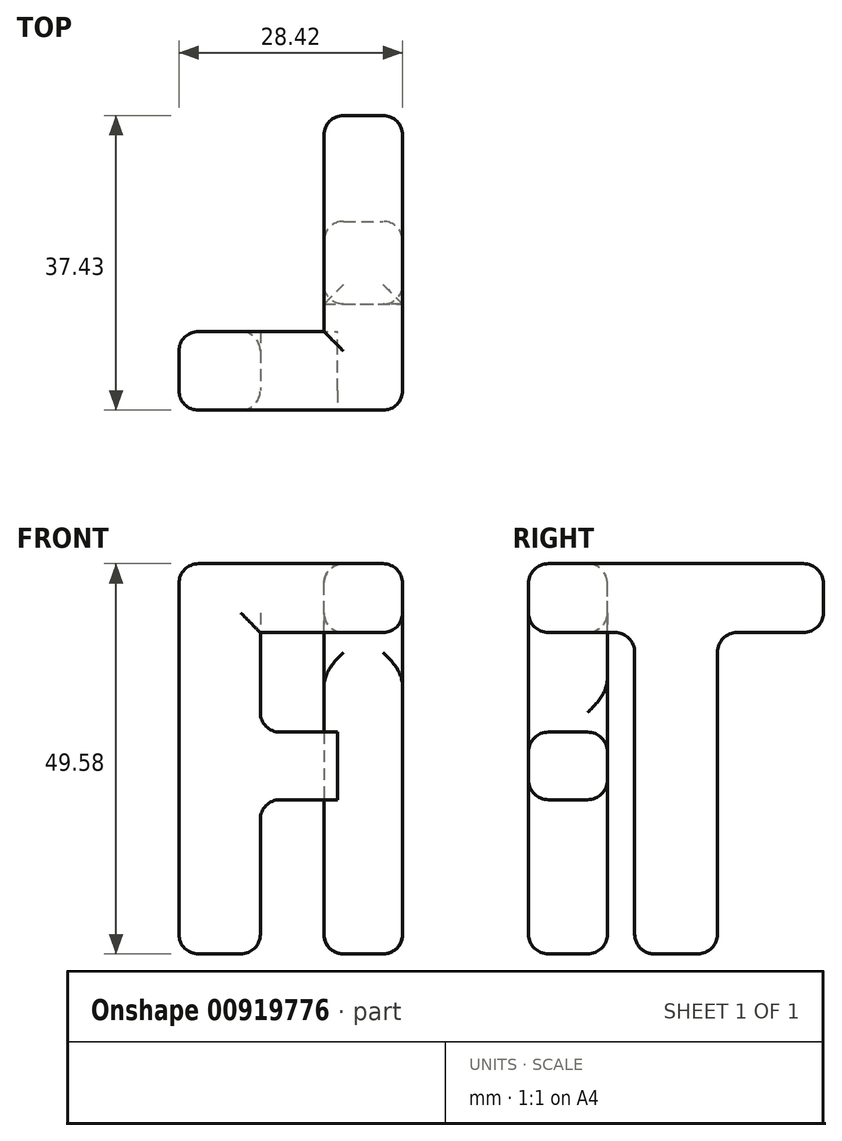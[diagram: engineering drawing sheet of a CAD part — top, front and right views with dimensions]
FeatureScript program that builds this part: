
annotation { "Feature Type Name" : "Feature", "Feature Type Description" : "" }
export const myFeature = defineFeature(function(context is Context, id is Id, definition is map)
    precondition{}
    {
        {
            var Q0;
            Q0=qCreatedBy(makeId("Front.planeOp"),FACE);
            var sketch = newSketch(context, id + "F0", { "sketchPlane" : qUnion([Q0])});
            skText(sketch, "E0", { "text": "F", "fontName": "NotoSans-Bold.ttf"});
            const initialGuessF0  = {"E0": [-0.03238, -0.0213, 1, 0, 0.05]};
            skSetInitialGuess(sketch, initialGuessF0);
            skSolve(sketch);
        }
        {
            var Q0;
            Q0=makeQuery(id+"F0.imprint","IMPRINT",FACE,{"disambiguationData":[TD([[makeQuery(id+"F0.imprint","IMPRINT",EDGE,{"derivedFrom":sQuery(id+"F0.wireOp",EDGE,"E0.sketch_text.stroke-0")}),-1.0]])]});
            extrude(context, id + "F1", {"entities" : qUnion([Q0]), "depth" : -10 * mm, "offsetDistance" : 25 * mm});
        }
        {
            var Q0;
            Q0=qCreatedBy(makeId("Right.planeOp"),FACE);
            var sketch = newSketch(context, id + "F2", { "sketchPlane" : qUnion([Q0])});
            skText(sketch, "E1", { "text": "T", "fontName": "OpenSans-Bold.ttf"});
            const initialGuessF2  = {"E1": [0.02709, -0.02241, 1, 0, 0.05]};
            skSetInitialGuess(sketch, initialGuessF2);
            skSolve(sketch);
        }
        {
            var Q0;
            Q0 = qSketchRegion(id + "F2", true);
            extrude(context, id + "F3", {"entities" : qUnion([Q0]), "depth" : -10 * mm, "offsetDistance" : 25 * mm});
        }
        {
            var Q0;
            Q0=makeQuery(id+"F3.opExtrude","SWEPT_BODY",BODY,{"disambiguationData":[OSD([sQuery(id+"F2.wireOp",EDGE,"E1.sketch_text.stroke-0"),sQuery(id+"F2.wireOp",EDGE,"E1.sketch_text.stroke-1"),sQuery(id+"F2.wireOp",EDGE,"E1.sketch_text.stroke-2"),sQuery(id+"F2.wireOp",EDGE,"E1.sketch_text.stroke-3"),sQuery(id+"F2.wireOp",EDGE,"E1.sketch_text.stroke-4"),sQuery(id+"F2.wireOp",EDGE,"E1.sketch_text.stroke-5"),sQuery(id+"F2.wireOp",EDGE,"E1.sketch_text.stroke-6"),sQuery(id+"F2.wireOp",EDGE,"E1.sketch_text.stroke-7")])]});
            var Q1;
            Q1=makeQuery(id+"F3.opExtrude","CAP_VERTEX",VERTEX,{"disambiguationData":[OSD([sQuery(id+"F2.wireOp",EDGE,"E1.sketch_text.stroke-3"),sQuery(id+"F2.wireOp",EDGE,"E1.sketch_text.stroke-4")])],"isStart":true});
            var Q2;
            Q2=makeQuery(id+"F1.opExtrude","CAP_VERTEX",VERTEX,{"disambiguationData":[OSD([sQuery(id+"F0.wireOp",EDGE,"E0.sketch_text.stroke-2"),sQuery(id+"F0.wireOp",EDGE,"E0.sketch_text.stroke-3")])],"isStart":true});
            transform(context, id + "F4", {"entities" : qUnion([Q0]), "transformType" : TransformType.TRANSLATION_ENTITY, "oppositeDirectionEntity" : false, "transformLine" : qUnion([Q1, Q2]), "makeCopy" : false});
        }
        {
            var Q0;
            Q0=makeQuery(id+"F1.opExtrude","SWEPT_FACE",FACE,{"disambiguationData":[OSD([sQuery(id+"F0.wireOp",EDGE,"E0.sketch_text.stroke-7")])]});
            var sketch = newSketch(context, id + "F5", { "sketchPlane" : qUnion([Q0])});
            skLineSegment(sketch, "E2.bottom", {"start": v(0, 6.88) * mm, "end": v(10, 6.88) * mm});
            skLineSegment(sketch, "E2.top", {"start": v(0, -1.7) * mm, "end": v(10, -1.7) * mm});
            skLineSegment(sketch, "E2.left", {"start": v(0, 6.88) * mm, "end": v(0, -1.7) * mm});
            skLineSegment(sketch, "E2.right", {"start": v(10, 6.88) * mm, "end": v(10, -1.7) * mm});
            skSolve(sketch);
        }
        {
            var Q0;
            Q0 = qSketchRegion(id + "F5", true);
            extrude(context, id + "F6", {"entities" : qUnion([Q0]), "depth" : -7 * mm, "offsetDistance" : 25 * mm});
        }
        {
            var Q0;
            Q0=makeQuery(id+"F6.opExtrude","SWEPT_BODY",BODY,{"disambiguationData":[OSD([sQuery(id+"F5.wireOp",EDGE,"E2.bottom"),sQuery(id+"F5.wireOp",EDGE,"E2.top"),sQuery(id+"F5.wireOp",EDGE,"E2.left"),sQuery(id+"F5.wireOp",EDGE,"E2.right")])]});
            var Q1;
            Q1=makeQuery(id+"F1.opExtrude","SWEPT_BODY",BODY,{"disambiguationData":[OSD([sQuery(id+"F0.wireOp",EDGE,"E0.sketch_text.stroke-0"),sQuery(id+"F0.wireOp",EDGE,"E0.sketch_text.stroke-1"),sQuery(id+"F0.wireOp",EDGE,"E0.sketch_text.stroke-2"),sQuery(id+"F0.wireOp",EDGE,"E0.sketch_text.stroke-3"),sQuery(id+"F0.wireOp",EDGE,"E0.sketch_text.stroke-4"),sQuery(id+"F0.wireOp",EDGE,"E0.sketch_text.stroke-5"),sQuery(id+"F0.wireOp",EDGE,"E0.sketch_text.stroke-6"),sQuery(id+"F0.wireOp",EDGE,"E0.sketch_text.stroke-7"),sQuery(id+"F0.wireOp",EDGE,"E0.sketch_text.stroke-8"),sQuery(id+"F0.wireOp",EDGE,"E0.sketch_text.stroke-9")])]});
            booleanBodies(context, id + "F7", {"operationType" : BooleanOperationType.SUBTRACTION, "tools" : qUnion([Q0]), "targets" : qUnion([Q1])});
        }
        {
            var Q0;
            Q0=makeQuery(id+"F1.opExtrude","SWEPT_BODY",BODY,{"disambiguationData":[OSD([sQuery(id+"F0.wireOp",EDGE,"E0.sketch_text.stroke-0"),sQuery(id+"F0.wireOp",EDGE,"E0.sketch_text.stroke-1"),sQuery(id+"F0.wireOp",EDGE,"E0.sketch_text.stroke-2"),sQuery(id+"F0.wireOp",EDGE,"E0.sketch_text.stroke-3"),sQuery(id+"F0.wireOp",EDGE,"E0.sketch_text.stroke-4"),sQuery(id+"F0.wireOp",EDGE,"E0.sketch_text.stroke-5"),sQuery(id+"F0.wireOp",EDGE,"E0.sketch_text.stroke-6"),sQuery(id+"F0.wireOp",EDGE,"E0.sketch_text.stroke-7"),sQuery(id+"F0.wireOp",EDGE,"E0.sketch_text.stroke-8"),sQuery(id+"F0.wireOp",EDGE,"E0.sketch_text.stroke-9")])]});
            var Q1;
            Q1=makeQuery(id+"F3.opExtrude","SWEPT_BODY",BODY,{"disambiguationData":[OSD([sQuery(id+"F2.wireOp",EDGE,"E1.sketch_text.stroke-0"),sQuery(id+"F2.wireOp",EDGE,"E1.sketch_text.stroke-1"),sQuery(id+"F2.wireOp",EDGE,"E1.sketch_text.stroke-2"),sQuery(id+"F2.wireOp",EDGE,"E1.sketch_text.stroke-3"),sQuery(id+"F2.wireOp",EDGE,"E1.sketch_text.stroke-4"),sQuery(id+"F2.wireOp",EDGE,"E1.sketch_text.stroke-5"),sQuery(id+"F2.wireOp",EDGE,"E1.sketch_text.stroke-6"),sQuery(id+"F2.wireOp",EDGE,"E1.sketch_text.stroke-7")])]});
            booleanBodies(context, id + "F8", {"operationType" : BooleanOperationType.UNION, "tools" : qUnion([Q0, Q1])});
        }
        {
            var Q0;
            Q0=makeQuery(id+"F1.opExtrude","SWEPT_FACE",FACE,{"disambiguationData":[OSD([sQuery(id+"F0.wireOp",EDGE,"E0.sketch_text.stroke-4")])]});
            var sketch = newSketch(context, id + "F9", { "sketchPlane" : qUnion([Q0])});
            skLineSegment(sketch, "E3.bottom", {"start": v(-15.8, -10) * mm, "end": v(-7.72, -10) * mm});
            skLineSegment(sketch, "E3.top", {"start": v(-15.8, 0) * mm, "end": v(-7.72, 0) * mm});
            skLineSegment(sketch, "E3.left", {"start": v(-15.8, -10) * mm, "end": v(-15.8, 0) * mm});
            skLineSegment(sketch, "E3.right", {"start": v(-7.72, -10) * mm, "end": v(-7.72, 0) * mm});
            skSolve(sketch);
        }
        {
            var Q0;
            Q0=makeQuery(id+"F9.imprint","IMPRINT",FACE,{"disambiguationData":[TD([[makeQuery(id+"F9.imprint","IMPRINT",EDGE,{"derivedFrom":sQuery(id+"F9.wireOp",EDGE,"E3.bottom")}),-1.0]])]});
            var Q1;
            Q1=makeQuery(id+"F3.opExtrude","SWEPT_FACE",FACE,{"disambiguationData":[OSD([sQuery(id+"F2.wireOp",EDGE,"E1.sketch_text.stroke-2")])]});
            extrude(context, id + "F10", {"entities" : qUnion([Q0]), "operationType" : NewBodyOperationType.ADD, "endBound" : BoundingType.UP_TO_SURFACE, "depth" : 25 * mm, "endBoundEntityFace" : qUnion([Q1]), "offsetDistance" : 25 * mm});
        }
        {
            var Q0;
            Q0=makeQuery(id+"F10.boolean.opBoolean","MERGE",EDGE,{"derivedFrom":[makeQuery(id+"F3.opExtrude","SWEPT_EDGE",EDGE,{"disambiguationData":[OSD([sQuery(id+"F2.wireOp",EDGE,"E1.sketch_text.stroke-2"),sQuery(id+"F2.wireOp",EDGE,"E1.sketch_text.stroke-3")])]}),makeQuery(id+"F10.opExtrude","CAP_EDGE",EDGE,{"disambiguationData":[OSD([sQuery(id+"F9.wireOp",EDGE,"E3.top")])],"isStart":false})]});
            var Q1;
            Q1=makeQuery(id+"F1.opExtrude","CAP_EDGE",EDGE,{"disambiguationData":[OSD([sQuery(id+"F0.wireOp",EDGE,"E0.sketch_text.stroke-5")])],"isStart":true});
            var Q2;
            Q2=makeQuery(id+"F3.opExtrude","CAP_EDGE",EDGE,{"disambiguationData":[OSD([sQuery(id+"F2.wireOp",EDGE,"E1.sketch_text.stroke-2")])],"isStart":true});
            var Q3;
            Q3=makeQuery(id+"F3.opExtrude","SWEPT_EDGE",EDGE,{"disambiguationData":[OSD([sQuery(id+"F2.wireOp",EDGE,"E1.sketch_text.stroke-1"),sQuery(id+"F2.wireOp",EDGE,"E1.sketch_text.stroke-2")])]});
            var Q4;
            Q4=makeQuery(id+"F10.opExtrude","CAP_EDGE",EDGE,{"disambiguationData":[OSD([sQuery(id+"F9.wireOp",EDGE,"E3.bottom")])],"isStart":false});
            var Q5;
            Q5=makeQuery(id+"F3.opExtrude","CAP_EDGE",EDGE,{"disambiguationData":[OSD([sQuery(id+"F2.wireOp",EDGE,"E1.sketch_text.stroke-2")])],"isStart":false});
            var Q6;
            Q6=makeQuery(id+"F10.opExtrude","CAP_EDGE",EDGE,{"disambiguationData":[OSD([sQuery(id+"F9.wireOp",EDGE,"E3.left")])],"isStart":false});
            var Q7;
            Q7=makeQuery(id+"F8.opBoolean","MERGE",EDGE,{"derivedFrom":[makeQuery(id+"F1.opExtrude","CAP_EDGE",EDGE,{"disambiguationData":[OSD([sQuery(id+"F0.wireOp",EDGE,"E0.sketch_text.stroke-3")])],"isStart":true}),makeQuery(id+"F3.opExtrude","CAP_EDGE",EDGE,{"disambiguationData":[OSD([sQuery(id+"F2.wireOp",EDGE,"E1.sketch_text.stroke-3")])],"isStart":true})]});
            var Q8;
            Q8=makeQuery(id+"F1.opExtrude","CAP_EDGE",EDGE,{"disambiguationData":[OSD([sQuery(id+"F0.wireOp",EDGE,"E0.sketch_text.stroke-2")])],"isStart":true});
            var Q9;
            Q9=makeQuery(id+"F8.opBoolean","MERGE",EDGE,{"derivedFrom":[makeQuery(id+"F1.opExtrude","SWEPT_EDGE",EDGE,{"disambiguationData":[OSD([sQuery(id+"F0.wireOp",EDGE,"E0.sketch_text.stroke-2"),sQuery(id+"F0.wireOp",EDGE,"E0.sketch_text.stroke-3")])]}),makeQuery(id+"F3.opExtrude","CAP_EDGE",EDGE,{"disambiguationData":[OSD([sQuery(id+"F2.wireOp",EDGE,"E1.sketch_text.stroke-4")])],"isStart":true})]});
            var Q10;
            Q10=makeQuery(id+"F3.opExtrude","CAP_EDGE",EDGE,{"disambiguationData":[OSD([sQuery(id+"F2.wireOp",EDGE,"E1.sketch_text.stroke-4")])],"isStart":false});
            var Q11;
            Q11=makeQuery(id+"F1.opExtrude","CAP_EDGE",EDGE,{"disambiguationData":[OSD([sQuery(id+"F0.wireOp",EDGE,"E0.sketch_text.stroke-2")])],"isStart":false});
            var Q12;
            Q12=makeQuery(id+"F1.opExtrude","SWEPT_EDGE",EDGE,{"disambiguationData":[OSD([sQuery(id+"F0.wireOp",EDGE,"E0.sketch_text.stroke-1"),sQuery(id+"F0.wireOp",EDGE,"E0.sketch_text.stroke-2")])]});
            var Q13;
            Q13=makeQuery(id+"F3.opExtrude","SWEPT_EDGE",EDGE,{"disambiguationData":[OSD([sQuery(id+"F2.wireOp",EDGE,"E1.sketch_text.stroke-4"),sQuery(id+"F2.wireOp",EDGE,"E1.sketch_text.stroke-5")])]});
            var Q14;
            Q14=makeQuery(id+"F3.opExtrude","CAP_EDGE",EDGE,{"disambiguationData":[OSD([sQuery(id+"F2.wireOp",EDGE,"E1.sketch_text.stroke-5")])],"isStart":true});
            var Q15;
            Q15=makeQuery(id+"F3.opExtrude","CAP_EDGE",EDGE,{"disambiguationData":[OSD([sQuery(id+"F2.wireOp",EDGE,"E1.sketch_text.stroke-6")])],"isStart":true});
            var Q16;
            Q16=makeQuery(id+"F3.opExtrude","CAP_EDGE",EDGE,{"disambiguationData":[OSD([sQuery(id+"F2.wireOp",EDGE,"E1.sketch_text.stroke-7")])],"isStart":true});
            var Q17;
            Q17=makeQuery(id+"F3.opExtrude","CAP_EDGE",EDGE,{"disambiguationData":[OSD([sQuery(id+"F2.wireOp",EDGE,"E1.sketch_text.stroke-0")])],"isStart":true});
            var Q18;
            Q18=makeQuery(id+"F3.opExtrude","SWEPT_EDGE",EDGE,{"disambiguationData":[OSD([sQuery(id+"F2.wireOp",EDGE,"E1.sketch_text.stroke-0"),sQuery(id+"F2.wireOp",EDGE,"E1.sketch_text.stroke-1")])]});
            var Q19;
            Q19=makeQuery(id+"F3.opExtrude","CAP_EDGE",EDGE,{"disambiguationData":[OSD([sQuery(id+"F2.wireOp",EDGE,"E1.sketch_text.stroke-0")])],"isStart":false});
            var Q20;
            Q20=makeQuery(id+"F3.opExtrude","SWEPT_EDGE",EDGE,{"disambiguationData":[OSD([sQuery(id+"F2.wireOp",EDGE,"E1.sketch_text.stroke-0"),sQuery(id+"F2.wireOp",EDGE,"E1.sketch_text.stroke-7")])]});
            var Q21;
            Q21=makeQuery(id+"F3.opExtrude","CAP_EDGE",EDGE,{"disambiguationData":[OSD([sQuery(id+"F2.wireOp",EDGE,"E1.sketch_text.stroke-7")])],"isStart":false});
            var Q22;
            Q22=makeQuery(id+"F3.opExtrude","CAP_EDGE",EDGE,{"disambiguationData":[OSD([sQuery(id+"F2.wireOp",EDGE,"E1.sketch_text.stroke-5")])],"isStart":false});
            var Q23;
            Q23=makeQuery(id+"F3.opExtrude","SWEPT_EDGE",EDGE,{"disambiguationData":[OSD([sQuery(id+"F2.wireOp",EDGE,"E1.sketch_text.stroke-5"),sQuery(id+"F2.wireOp",EDGE,"E1.sketch_text.stroke-6")])]});
            var Q24;
            Q24=makeQuery(id+"F3.opExtrude","CAP_EDGE",EDGE,{"disambiguationData":[OSD([sQuery(id+"F2.wireOp",EDGE,"E1.sketch_text.stroke-6")])],"isStart":false});
            var Q25;
            Q25=makeQuery(id+"F3.opExtrude","SWEPT_EDGE",EDGE,{"disambiguationData":[OSD([sQuery(id+"F2.wireOp",EDGE,"E1.sketch_text.stroke-6"),sQuery(id+"F2.wireOp",EDGE,"E1.sketch_text.stroke-7")])]});
            fillet(context, id + "F11", {"entities" : qUnion([Q0, Q1, Q2, Q3, Q4, Q5, Q6, Q7, Q8, Q9, Q10, Q11, Q12, Q13, Q14, Q15, Q16, Q17, Q18, Q19, Q20, Q21, Q22, Q23, Q24, Q25]), "radius" : 2.5 * mm, "tangentPropagation" : true, "allowEdgeOverflow" : false});
        }
        {
            var Q0;
            Q0=makeQuery(id+"F1.opExtrude","CAP_EDGE",EDGE,{"disambiguationData":[OSD([sQuery(id+"F0.wireOp",EDGE,"E0.sketch_text.stroke-6")])],"isStart":true});
            var Q1;
            Q1=makeQuery(id+"F1.opExtrude","SWEPT_EDGE",EDGE,{"disambiguationData":[OSD([sQuery(id+"F0.wireOp",EDGE,"E0.sketch_text.stroke-5"),sQuery(id+"F0.wireOp",EDGE,"E0.sketch_text.stroke-6")])]});
            var Q2;
            Q2=makeQuery(id+"F1.opExtrude","CAP_EDGE",EDGE,{"disambiguationData":[OSD([sQuery(id+"F0.wireOp",EDGE,"E0.sketch_text.stroke-6")])],"isStart":false});
            var Q3;
            Q3=makeQuery(id+"F7.opBoolean","COPY",EDGE,{"derivedFrom":makeQuery(id+"F6.opExtrude","CAP_EDGE",EDGE,{"disambiguationData":[OSD([sQuery(id+"F5.wireOp",EDGE,"E2.right")])],"isStart":false})});
            var Q4;
            Q4=makeQuery(id+"F7.opBoolean","COPY",EDGE,{"derivedFrom":makeQuery(id+"F6.opExtrude","CAP_EDGE",EDGE,{"disambiguationData":[OSD([sQuery(id+"F5.wireOp",EDGE,"E2.top")])],"isStart":false})});
            var Q5;
            Q5=makeQuery(id+"F7.opBoolean","COPY",EDGE,{"derivedFrom":makeQuery(id+"F6.opExtrude","CAP_EDGE",EDGE,{"disambiguationData":[OSD([sQuery(id+"F5.wireOp",EDGE,"E2.left")])],"isStart":false})});
            var Q6;
            Q6=makeQuery(id+"F1.opExtrude","CAP_EDGE",EDGE,{"disambiguationData":[OSD([sQuery(id+"F0.wireOp",EDGE,"E0.sketch_text.stroke-8")])],"isStart":true});
            var Q7;
            Q7=makeQuery(id+"F1.opExtrude","CAP_EDGE",EDGE,{"disambiguationData":[OSD([sQuery(id+"F0.wireOp",EDGE,"E0.sketch_text.stroke-8")])],"isStart":false});
            var Q8;
            Q8=makeQuery(id+"F1.opExtrude","CAP_EDGE",EDGE,{"disambiguationData":[OSD([sQuery(id+"F0.wireOp",EDGE,"E0.sketch_text.stroke-9")])],"isStart":true});
            var Q9;
            Q9=makeQuery(id+"F1.opExtrude","CAP_EDGE",EDGE,{"disambiguationData":[OSD([sQuery(id+"F0.wireOp",EDGE,"E0.sketch_text.stroke-9")])],"isStart":false});
            var Q10;
            Q10=makeQuery(id+"F1.opExtrude","SWEPT_EDGE",EDGE,{"disambiguationData":[OSD([sQuery(id+"F0.wireOp",EDGE,"E0.sketch_text.stroke-8"),sQuery(id+"F0.wireOp",EDGE,"E0.sketch_text.stroke-9")])]});
            var Q11;
            Q11=makeQuery(id+"F1.opExtrude","SWEPT_EDGE",EDGE,{"disambiguationData":[OSD([sQuery(id+"F0.wireOp",EDGE,"E0.sketch_text.stroke-0"),sQuery(id+"F0.wireOp",EDGE,"E0.sketch_text.stroke-9")])]});
            var Q12;
            Q12=makeQuery(id+"F1.opExtrude","CAP_EDGE",EDGE,{"disambiguationData":[OSD([sQuery(id+"F0.wireOp",EDGE,"E0.sketch_text.stroke-0")])],"isStart":true});
            var Q13;
            Q13=makeQuery(id+"F1.opExtrude","CAP_EDGE",EDGE,{"disambiguationData":[OSD([sQuery(id+"F0.wireOp",EDGE,"E0.sketch_text.stroke-0")])],"isStart":false});
            var Q14;
            Q14=makeQuery(id+"F1.opExtrude","SWEPT_EDGE",EDGE,{"disambiguationData":[OSD([sQuery(id+"F0.wireOp",EDGE,"E0.sketch_text.stroke-0"),sQuery(id+"F0.wireOp",EDGE,"E0.sketch_text.stroke-1")])]});
            var Q15;
            Q15=makeQuery(id+"F1.opExtrude","CAP_EDGE",EDGE,{"disambiguationData":[OSD([sQuery(id+"F0.wireOp",EDGE,"E0.sketch_text.stroke-1")])],"isStart":true});
            var Q16;
            Q16=makeQuery(id+"F1.opExtrude","CAP_EDGE",EDGE,{"disambiguationData":[OSD([sQuery(id+"F0.wireOp",EDGE,"E0.sketch_text.stroke-1")])],"isStart":false});
            var Q17;
            Q17=makeQuery(id+"F7.opBoolean","COPY",EDGE,{"derivedFrom":makeQuery(id+"F6.opExtrude","CAP_EDGE",EDGE,{"disambiguationData":[OSD([sQuery(id+"F5.wireOp",EDGE,"E2.bottom")])],"isStart":false})});
            fillet(context, id + "F12", {"entities" : qUnion([Q0, Q1, Q2, Q3, Q4, Q5, Q6, Q7, Q8, Q9, Q10, Q11, Q12, Q13, Q14, Q15, Q16, Q17]), "radius" : 2.5 * mm, "tangentPropagation" : true, "allowEdgeOverflow" : false});
        }
    });
